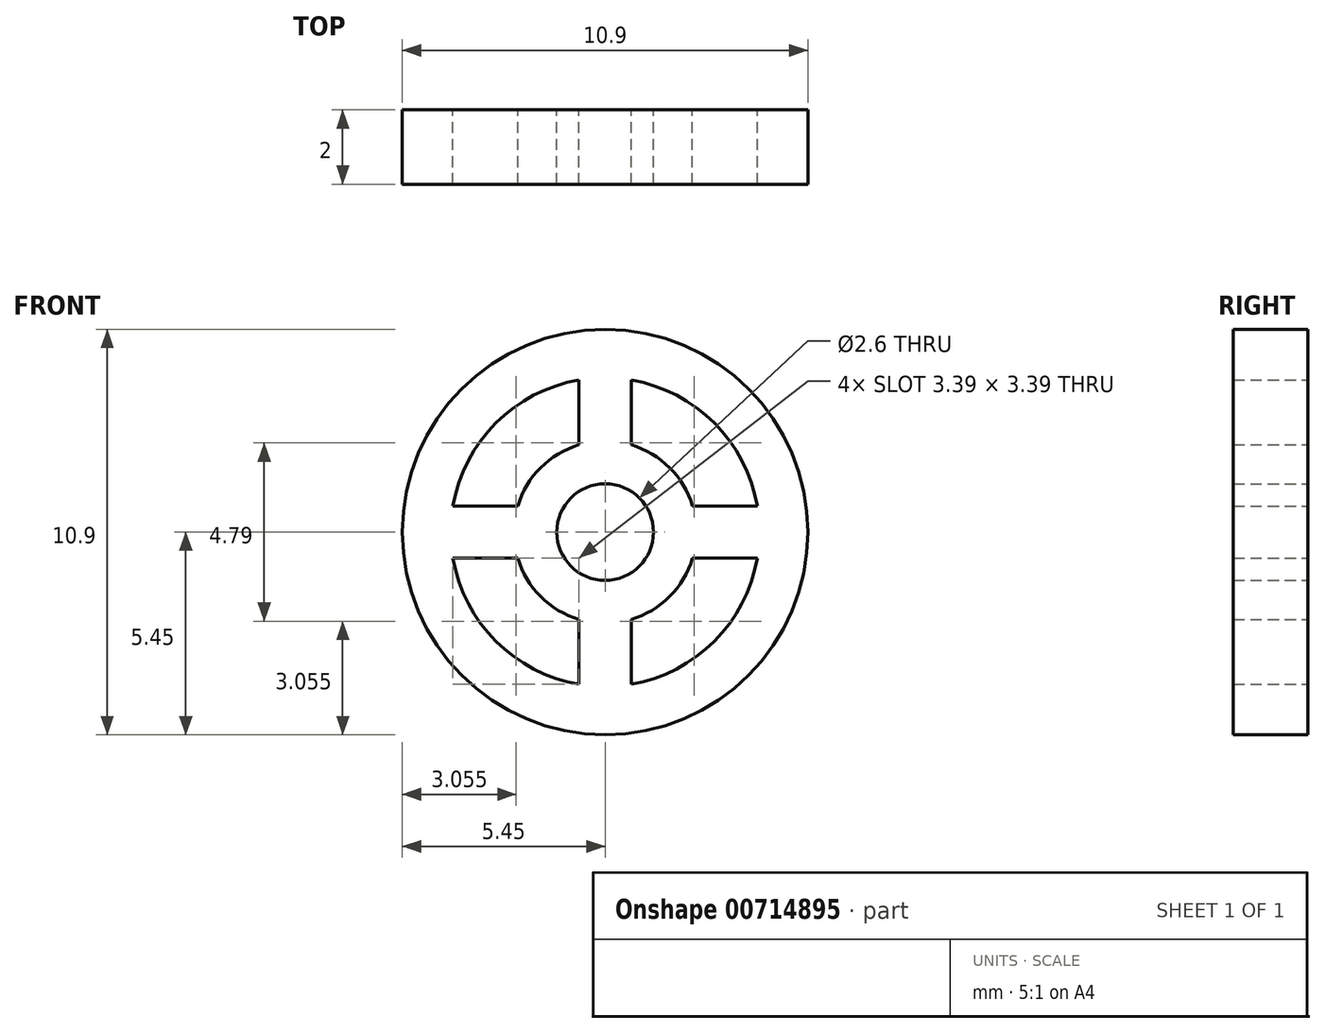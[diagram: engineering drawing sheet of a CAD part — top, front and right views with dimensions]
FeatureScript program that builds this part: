
annotation { "Feature Type Name" : "Feature", "Feature Type Description" : "" }
export const myFeature = defineFeature(function(context is Context, id is Id, definition is map)
    precondition{}
    {
        {
            var Q0;
            Q0=qCreatedBy(makeId("Front.planeOp"),FACE);
            var sketch = newSketch(context, id + "F0", { "sketchPlane" : qUnion([Q0])});
            skCircle(sketch, "E0", {"center": v(0, 0) * mm, "radius": 5.45 * mm});
            skCircle(sketch, "E1", {"center": v(0, 0) * mm, "radius": 4.15 * mm});
            skCircle(sketch, "E2", {"center": v(0, 0) * mm, "radius": 2.45 * mm});
            skCircle(sketch, "E3", {"center": v(0, 0) * mm, "radius": 1.3 * mm});
            skPoint(sketch, "E4.start.orphan", {"position": v(0, 2.45) * mm});
            skPoint(sketch, "E5.start.orphan", {"position": v(0, -2.45) * mm});
            skPoint(sketch, "E6.start.orphan", {"position": v(-2.45, 0) * mm});
            skPoint(sketch, "E7.start.orphan", {"position": v(2.45, 0) * mm});
            skPoint(sketch, "E8.start.orphan", {"position": v(-1.27, 2.1) * mm});
            skPoint(sketch, "E9.start.orphan", {"position": v(-2.35, 0.7) * mm});
            skPoint(sketch, "E10.start.orphan", {"position": v(2.35, 0.7) * mm});
            skPoint(sketch, "E11.start.orphan", {"position": v(1.27, 2.1) * mm});
            skLineSegment(sketch, "E12", {"start": v(0, 4.15) * mm, "end": v(0, 2.45) * mm});
            skLineSegment(sketch, "E13", {"start": v(2.45, 0) * mm, "end": v(4.15, 0) * mm});
            skLineSegment(sketch, "E14", {"start": v(0, -2.45) * mm, "end": v(0, -4.15) * mm});
            skLineSegment(sketch, "E15", {"start": v(-2.45, 0) * mm, "end": v(-4.15, 0) * mm});
            skLineSegment(sketch, "E16", {"start": v(-2.35, -0.7) * mm, "end": v(-4.1, -0.7) * mm});
            skLineSegment(sketch, "E17", {"start": v(-2.35, 0.7) * mm, "end": v(-4.1, 0.7) * mm});
            skLineSegment(sketch, "E18", {"start": v(-0.7, 2.35) * mm, "end": v(-0.7, 4.1) * mm});
            skLineSegment(sketch, "E19", {"start": v(0.7, 2.35) * mm, "end": v(0.7, 4.1) * mm});
            skLineSegment(sketch, "E20", {"start": v(2.35, 0.7) * mm, "end": v(4.1, 0.7) * mm});
            skLineSegment(sketch, "E21", {"start": v(2.35, -0.7) * mm, "end": v(4.1, -0.7) * mm});
            skLineSegment(sketch, "E22", {"start": v(0.7, -2.35) * mm, "end": v(0.7, -4.1) * mm});
            skLineSegment(sketch, "E23", {"start": v(-0.7, -2.35) * mm, "end": v(-0.7, -4.1) * mm});
            skSolve(sketch);
        }
        {
            var Q0;
            Q0 = qSketchRegion(id + "F0", true);
            var Q1;
            Q1=makeQuery(id+"F0.imprint","IMPRINT",FACE,{"disambiguationData":[TD([[makeQuery(id+"F0.imprint","IMPRINT",EDGE,{"derivedFrom":sQuery(id+"F0.wireOp",EDGE,"E3")}),-1.0]])]});
            var Q2;
            {var subQ0=sQuery(id+"F0.wireOp",EDGE,"E15");Q2=makeQuery(id+"F0.imprint","IMPRINT",FACE,{"disambiguationData":[TD([[makeQuery(id+"F0.imprint","IMPRINT",EDGE,{"derivedFrom":subQ0}),-1.0]])]});}
            var Q3;
            {var subQ0=sQuery(id+"F0.wireOp",EDGE,"E15");Q3=makeQuery(id+"F0.imprint","IMPRINT",FACE,{"disambiguationData":[TD([[makeQuery(id+"F0.imprint","IMPRINT",EDGE,{"derivedFrom":subQ0}),1.0]])]});}
            var Q4;
            {var subQ0=sQuery(id+"F0.wireOp",EDGE,"E14");Q4=makeQuery(id+"F0.imprint","IMPRINT",FACE,{"disambiguationData":[TD([[makeQuery(id+"F0.imprint","IMPRINT",EDGE,{"derivedFrom":subQ0}),-1.0]])]});}
            var Q5;
            {var subQ0=sQuery(id+"F0.wireOp",EDGE,"E14");Q5=makeQuery(id+"F0.imprint","IMPRINT",FACE,{"disambiguationData":[TD([[makeQuery(id+"F0.imprint","IMPRINT",EDGE,{"derivedFrom":subQ0}),1.0]])]});}
            var Q6;
            {var subQ0=sQuery(id+"F0.wireOp",EDGE,"E13");Q6=makeQuery(id+"F0.imprint","IMPRINT",FACE,{"disambiguationData":[TD([[makeQuery(id+"F0.imprint","IMPRINT",EDGE,{"derivedFrom":subQ0}),-1.0]])]});}
            var Q7;
            {var subQ0=sQuery(id+"F0.wireOp",EDGE,"E12");Q7=makeQuery(id+"F0.imprint","IMPRINT",FACE,{"disambiguationData":[TD([[makeQuery(id+"F0.imprint","IMPRINT",EDGE,{"derivedFrom":subQ0}),-1.0]])]});}
            var Q8;
            {var subQ0=sQuery(id+"F0.wireOp",EDGE,"E12");Q8=makeQuery(id+"F0.imprint","IMPRINT",FACE,{"disambiguationData":[TD([[makeQuery(id+"F0.imprint","IMPRINT",EDGE,{"derivedFrom":subQ0}),1.0]])]});}
            var Q9;
            {var subQ0=sQuery(id+"F0.wireOp",EDGE,"E13");Q9=makeQuery(id+"F0.imprint","IMPRINT",FACE,{"disambiguationData":[TD([[makeQuery(id+"F0.imprint","IMPRINT",EDGE,{"derivedFrom":subQ0}),1.0]])]});}
            extrude(context, id + "F1", {"entities" : qUnion([Q0, Q1, Q2, Q3, Q4, Q5, Q6, Q7, Q8, Q9]), "depth" : 2 * mm, "offsetDistance" : 25 * mm});
        }
    });
